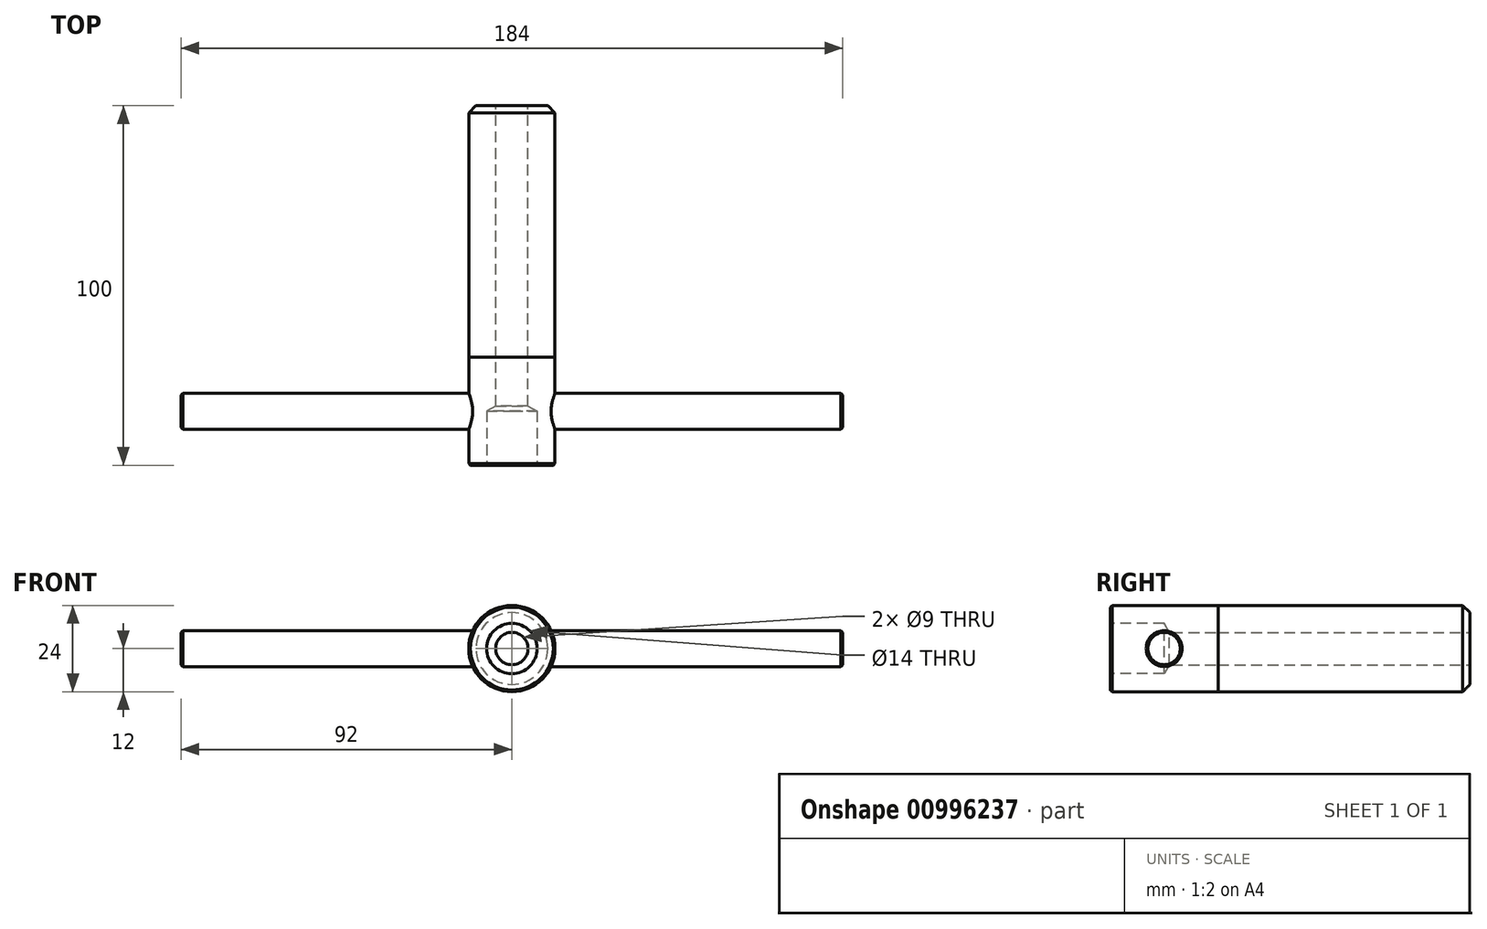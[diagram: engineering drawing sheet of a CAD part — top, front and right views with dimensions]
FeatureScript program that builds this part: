
annotation { "Feature Type Name" : "Feature", "Feature Type Description" : "" }
export const myFeature = defineFeature(function(context is Context, id is Id, definition is map)
    precondition{}
    {
        {
            var Q0;
            Q0=qCreatedBy(makeId("Front.planeOp"),FACE);
            var sketch = newSketch(context, id + "F0", { "sketchPlane" : qUnion([Q0])});
            skCircle(sketch, "E0", {"center": v(0, 0) * mm, "radius": 12 * mm});
            skSolve(sketch);
        }
        {
            var Q0;
            Q0=makeQuery(id+"F0.imprint","IMPRINT",FACE,{"disambiguationData":[TD([[makeQuery(id+"F0.imprint","IMPRINT",EDGE,{"derivedFrom":sQuery(id+"F0.wireOp",EDGE,"E0")}),1.0]])]});
            extrude(context, id + "F1", {"entities" : qUnion([Q0]), "surfaceOperationType" : NewSurfaceOperationType.ADD, "depth" : 30 * mm, "offsetDistance" : 25 * mm});
        }
        {
            var Q0;
            Q0=makeQuery(id+"F1.opExtrude","CAP_FACE",FACE,{"disambiguationData":[OSD([sQuery(id+"F0.wireOp",EDGE,"E0")])],"isStart":false});
            var sketch = newSketch(context, id + "F2", { "sketchPlane" : qUnion([Q0])});
            skCircle(sketch, "E1", {"center": v(0, 0) * mm, "radius": 2.5 * mm});
            skSolve(sketch);
        }
        {
            var Q0;
            Q0=makeQuery(id+"F1.opExtrude","CAP_FACE",FACE,{"disambiguationData":[OSD([sQuery(id+"F0.wireOp",EDGE,"E0")])],"isStart":true});
            extrude(context, id + "F3", {"entities" : qUnion([Q0]), "depth" : 70 * mm, "offsetDistance" : 25 * mm});
        }
        {
            var Q0;
            Q0 = qSketchRegion(id + "F2", true);
            extrude(context, id + "F4", {"entities" : qUnion([Q0]), "operationType" : NewBodyOperationType.REMOVE, "endBound" : BoundingType.THROUGH_ALL, "oppositeDirection" : true, "depth" : 25 * mm, "offsetDistance" : 25 * mm});
        }
        {
            var Q0;
            Q0=makeQuery(id+"F1.opExtrude","CAP_FACE",FACE,{"disambiguationData":[OSD([sQuery(id+"F0.wireOp",EDGE,"E0")])],"isStart":false});
            var sketch = newSketch(context, id + "F5", { "sketchPlane" : qUnion([Q0])});
            skPoint(sketch, "E2", {"position": v(0, 0) * mm});
            skSolve(sketch);
        }
        {
            var Q0;
            Q0=sQuery(id+"F5.wireOp",VERTEX,"E2");
            var Q1;
            Q1=makeQuery(id+"F1.opExtrude","SWEPT_BODY",BODY,{"disambiguationData":[OSD([sQuery(id+"F0.wireOp",EDGE,"E0")])]});
            hole(context, id + "F6", {"style" : HoleStyle.SIMPLE, "endStyle" : HoleEndStyle.BLIND, "standardTappedOrClearance" : lookupTablePath({ "standard" : "ISO", "engagement" : "75%", "pitch" : "2 mm", "size" : "M16", "type" : "Tapped" }), "standardBlindInLast" : lookupTablePath({ "standard" : "ISO", "fit" : "Normal", "engagement" : "75%", "pitch" : "2 mm", "size" : "M16", "type" : "Clearance & tapped" }), "holeDiameter" : 14 * mm, "majorDiameter" : 16 * mm, "showTappedDepth" : true, "holeDepth" : 15 * mm, "isTappedThrough" : true, "tappedDepth" : 9 * mm, "tapClearance" : 3, "locations" : qUnion([Q0]), "scope" : qUnion([Q1])});
        }
        {
            var Q0;
            Q0=qCreatedBy(makeId("Right.planeOp"),FACE);
            cPlane(context, id + "F7", {"entities" : qUnion([Q0]), "cplaneType" : CPlaneType.OFFSET, "offset" : 12 * mm, "width" : 150 * mm, "height" : 150 * mm});
        }
        {
            var Q0;
            Q0=qCreatedBy(id+"F7.planeOp",FACE);
            var sketch = newSketch(context, id + "F8", { "sketchPlane" : qUnion([Q0])});
            skCircle(sketch, "E3", {"center": v(-15, 0) * mm, "radius": 5 * mm});
            skSolve(sketch);
        }
        {
            var Q0;
            Q0=makeQuery(id+"F8.imprint","IMPRINT",FACE,{"disambiguationData":[TD([[makeQuery(id+"F8.imprint","IMPRINT",EDGE,{"derivedFrom":sQuery(id+"F8.wireOp",EDGE,"E3")}),1.0]])]});
            extrude(context, id + "F9", {"entities" : qUnion([Q0]), "operationType" : NewBodyOperationType.ADD, "depth" : 80 * mm, "offsetDistance" : 25 * mm, "hasSecondDirection" : true, "secondDirectionOppositeDirection" : true, "secondDirectionDepth" : 3 * mm});
        }
        {
            var Q0;
            Q0=qCreatedBy(makeId("Right.planeOp"),FACE);
            cPlane(context, id + "F10", {"entities" : qUnion([Q0]), "cplaneType" : CPlaneType.OFFSET, "offset" : 12 * mm, "oppositeDirection" : true, "width" : 150 * mm, "height" : 150 * mm});
        }
        {
            var Q0;
            Q0=qCreatedBy(id+"F10.planeOp",FACE);
            var sketch = newSketch(context, id + "F11", { "sketchPlane" : qUnion([Q0])});
            skCircle(sketch, "E4", {"center": v(-15, 0) * mm, "radius": 5 * mm});
            skSolve(sketch);
        }
        {
            var Q0;
            Q0=makeQuery(id+"F11.imprint","IMPRINT",FACE,{"disambiguationData":[TD([[makeQuery(id+"F11.imprint","IMPRINT",EDGE,{"derivedFrom":sQuery(id+"F11.wireOp",EDGE,"E4")}),1.0]])]});
            extrude(context, id + "F12", {"entities" : qUnion([Q0]), "operationType" : NewBodyOperationType.ADD, "oppositeDirection" : true, "depth" : 80 * mm, "offsetDistance" : 25 * mm, "hasSecondDirection" : true, "secondDirectionOppositeDirection" : false, "secondDirectionDepth" : 3 * mm});
        }
        {
            var Q0;
            Q0=makeQuery(id+"F9.opExtrude","CAP_EDGE",EDGE,{"disambiguationData":[OSD([sQuery(id+"F8.wireOp",EDGE,"E3")])],"isStart":false});
            var Q1;
            Q1=makeQuery(id+"F1.opExtrude","CAP_EDGE",EDGE,{"disambiguationData":[OSD([sQuery(id+"F0.wireOp",EDGE,"E0")])],"isStart":false});
            var Q2;
            Q2=makeQuery(id+"F12.opExtrude","CAP_EDGE",EDGE,{"disambiguationData":[OSD([sQuery(id+"F11.wireOp",EDGE,"E4")])],"isStart":false});
            chamfer(context, id + "F13", {"entities" : qUnion([Q0, Q1, Q2]), "width" : 0.5 * mm, "tangentPropagation" : true});
        }
        {
            var Q0;
            Q0=makeQuery(id+"F3.opExtrude","CAP_FACE",FACE,{"disambiguationData":[OSD([sQuery(id+"F0.wireOp",EDGE,"E0")])],"isStart":false});
            var sketch = newSketch(context, id + "F14", { "sketchPlane" : qUnion([Q0])});
            skCircle(sketch, "E5", {"center": v(0, 0) * mm, "radius": 4.5 * mm});
            skSolve(sketch);
        }
        {
            var Q0;
            Q0=makeQuery(id+"F14.imprint","IMPRINT",FACE,{"disambiguationData":[TD([[makeQuery(id+"F14.imprint","IMPRINT",EDGE,{"derivedFrom":sQuery(id+"F14.wireOp",EDGE,"E5")}),1.0]])]});
            extrude(context, id + "F15", {"entities" : qUnion([Q0]), "operationType" : NewBodyOperationType.ADD, "depth" : 16 * mm, "offsetDistance" : 25 * mm});
        }
        {
            var Q0;
            Q0=makeQuery(id+"F15.opExtrude","CAP_FACE",FACE,{"disambiguationData":[OSD([sQuery(id+"F14.wireOp",EDGE,"E5")])],"isStart":false});
            var sketch = newSketch(context, id + "F16", { "sketchPlane" : qUnion([Q0])});
            skCircle(sketch, "E6", {"center": v(0, 0) * mm, "radius": 2.5 * mm});
            skSolve(sketch);
        }
        {
            var Q0;
            Q0=makeQuery(id+"F16.imprint","IMPRINT",FACE,{"disambiguationData":[TD([[makeQuery(id+"F16.imprint","IMPRINT",EDGE,{"derivedFrom":sQuery(id+"F16.wireOp",EDGE,"E6")}),1.0]])]});
            extrude(context, id + "F17", {"entities" : qUnion([Q0]), "operationType" : NewBodyOperationType.REMOVE, "endBound" : BoundingType.THROUGH_ALL, "oppositeDirection" : true, "depth" : 25 * mm, "offsetDistance" : 25 * mm});
        }
        {
            var Q0;
            Q0=makeQuery(id+"F3.opExtrude","CAP_EDGE",EDGE,{"disambiguationData":[OSD([sQuery(id+"F0.wireOp",EDGE,"E0")])],"isStart":false});
            chamfer(context, id + "F18", {"entities" : qUnion([Q0]), "width" : 2 * mm, "tangentPropagation" : true});
        }
    });
